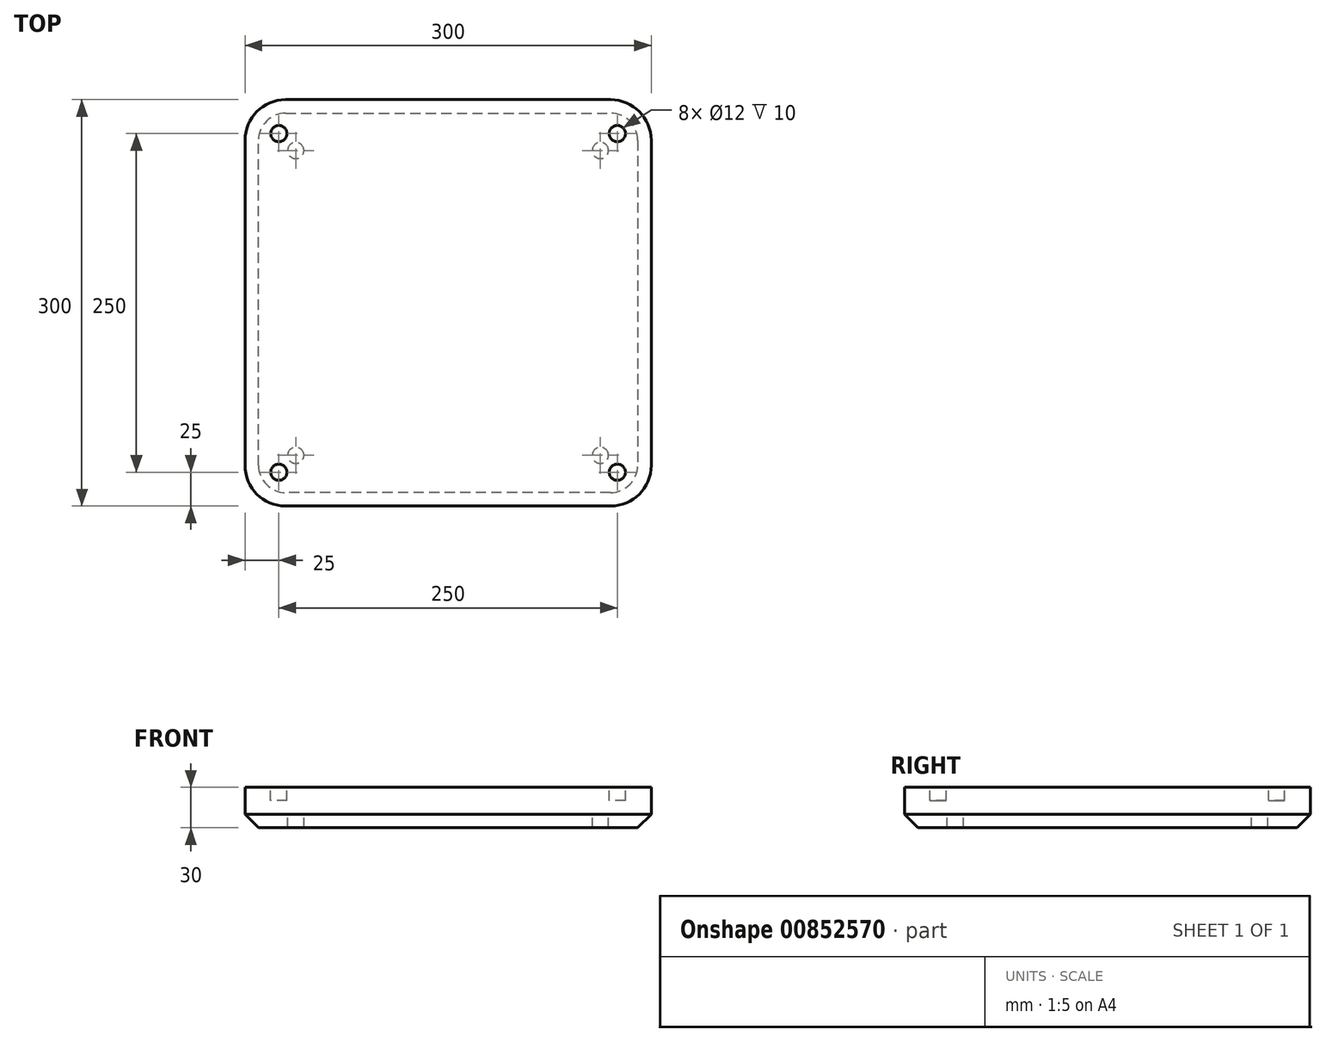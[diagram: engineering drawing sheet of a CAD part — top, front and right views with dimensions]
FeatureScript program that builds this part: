
annotation { "Feature Type Name" : "Feature", "Feature Type Description" : "" }
export const myFeature = defineFeature(function(context is Context, id is Id, definition is map)
    precondition{}
    {
        {
            var Q0;
            Q0=qCreatedBy(makeId("Top.planeOp"),FACE);
            var sketch = newSketch(context, id + "F0", { "sketchPlane" : qUnion([Q0])});
            skLineSegment(sketch, "E0.bottom", {"start": v(120, 150) * mm, "end": v(-120, 150) * mm});
            skLineSegment(sketch, "E0.top", {"start": v(120, -150) * mm, "end": v(-120, -150) * mm});
            skLineSegment(sketch, "E0.left", {"start": v(150, 120) * mm, "end": v(150, -120) * mm});
            skLineSegment(sketch, "E0.right", {"start": v(-150, 120) * mm, "end": v(-150, -120) * mm});
            skPoint(sketch, "E0.middle", {"position": v(0, 0) * mm});
            skPoint(sketch, "E1.visualSharp", {"position": v(-150, 150) * mm});
            skArc(sketch, "E1.filletArc", {"start": v(-120, 150) * mm, "mid": v(-141.21, 141.21) * mm, "end": v(-150, 120) * mm});
            skPoint(sketch, "E2.visualSharp", {"position": v(150, 150) * mm});
            skArc(sketch, "E2.filletArc", {"start": v(150, 120) * mm, "mid": v(141.21, 141.21) * mm, "end": v(120, 150) * mm});
            skPoint(sketch, "E3.visualSharp", {"position": v(150, -150) * mm});
            skArc(sketch, "E3.filletArc", {"start": v(120, -150) * mm, "mid": v(141.21, -141.21) * mm, "end": v(150, -120) * mm});
            skPoint(sketch, "E4.visualSharp", {"position": v(-150, -150) * mm});
            skArc(sketch, "E4.filletArc", {"start": v(-150, -120) * mm, "mid": v(-141.21, -141.21) * mm, "end": v(-120, -150) * mm});
            skCircle(sketch, "E5", {"center": v(-112.5, -112.5) * mm, "radius": 6 * mm});
            skCircle(sketch, "E6", {"center": v(-112.5, 112.5) * mm, "radius": 6 * mm});
            skCircle(sketch, "E7", {"center": v(112.5, 112.5) * mm, "radius": 6 * mm});
            skCircle(sketch, "E8", {"center": v(112.5, -112.5) * mm, "radius": 6 * mm});
            skCircle(sketch, "E9", {"center": v(125, 125) * mm, "radius": 6 * mm});
            skCircle(sketch, "E10", {"center": v(-125, 125) * mm, "radius": 6 * mm});
            skCircle(sketch, "E11", {"center": v(-125, -125) * mm, "radius": 6 * mm});
            skCircle(sketch, "E12", {"center": v(125, -125) * mm, "radius": 6 * mm});
            skSolve(sketch);
        }
        {
            var Q0;
            Q0=makeQuery(id+"F0.imprint","IMPRINT",FACE,{"disambiguationData":[TD([[makeQuery(id+"F0.imprint","IMPRINT",EDGE,{"derivedFrom":sQuery(id+"F0.wireOp",EDGE,"E0.bottom")}),1.0]])]});
            var Q1;
            Q1=makeQuery(id+"F0.imprint","IMPRINT",FACE,{"disambiguationData":[TD([[makeQuery(id+"F0.imprint","IMPRINT",EDGE,{"derivedFrom":sQuery(id+"F0.wireOp",EDGE,"E10")}),1.0]])]});
            var Q2;
            Q2=makeQuery(id+"F0.imprint","IMPRINT",FACE,{"disambiguationData":[TD([[makeQuery(id+"F0.imprint","IMPRINT",EDGE,{"derivedFrom":sQuery(id+"F0.wireOp",EDGE,"E9")}),1.0]])]});
            var Q3;
            Q3=makeQuery(id+"F0.imprint","IMPRINT",FACE,{"disambiguationData":[TD([[makeQuery(id+"F0.imprint","IMPRINT",EDGE,{"derivedFrom":sQuery(id+"F0.wireOp",EDGE,"E12")}),1.0]])]});
            var Q4;
            Q4=makeQuery(id+"F0.imprint","IMPRINT",FACE,{"disambiguationData":[TD([[makeQuery(id+"F0.imprint","IMPRINT",EDGE,{"derivedFrom":sQuery(id+"F0.wireOp",EDGE,"E11")}),1.0]])]});
            extrude(context, id + "F1", {"entities" : qUnion([Q0, Q1, Q2, Q3, Q4]), "oppositeDirection" : true, "depth" : 30 * mm, "offsetDistance" : 25 * mm});
        }
        {
            var Q0;
            Q0=makeQuery(id+"F1.opExtrude","CAP_EDGE",EDGE,{"disambiguationData":[OSD([sQuery(id+"F0.wireOp",EDGE,"E0.bottom")])],"isStart":false});
            chamfer(context, id + "F2", {"entities" : qUnion([Q0]), "chamferType" : ChamferType.OFFSET_ANGLE, "width" : 10 * mm, "oppositeDirection" : false, "angle" : 45 * degree, "tangentPropagation" : true});
        }
        {
            var Q0;
            Q0=makeQuery(id+"F0.imprint","IMPRINT",FACE,{"disambiguationData":[TD([[makeQuery(id+"F0.imprint","IMPRINT",EDGE,{"derivedFrom":sQuery(id+"F0.wireOp",EDGE,"E10")}),1.0]])]});
            var Q1;
            Q1=makeQuery(id+"F0.imprint","IMPRINT",FACE,{"disambiguationData":[TD([[makeQuery(id+"F0.imprint","IMPRINT",EDGE,{"derivedFrom":sQuery(id+"F0.wireOp",EDGE,"E9")}),1.0]])]});
            var Q2;
            Q2=makeQuery(id+"F0.imprint","IMPRINT",FACE,{"disambiguationData":[TD([[makeQuery(id+"F0.imprint","IMPRINT",EDGE,{"derivedFrom":sQuery(id+"F0.wireOp",EDGE,"E11")}),1.0]])]});
            var Q3;
            Q3=makeQuery(id+"F0.imprint","IMPRINT",FACE,{"disambiguationData":[TD([[makeQuery(id+"F0.imprint","IMPRINT",EDGE,{"derivedFrom":sQuery(id+"F0.wireOp",EDGE,"E12")}),1.0]])]});
            var Q4;
            Q4=sQuery(id+"F0.wireOp",EDGE,"E9");
            var Q5;
            Q5=sQuery(id+"F0.wireOp",EDGE,"E10");
            var Q6;
            Q6=sQuery(id+"F0.wireOp",EDGE,"E11");
            var Q7;
            Q7=sQuery(id+"F0.wireOp",EDGE,"E12");
            extrude(context, id + "F3", {"entities" : qUnion([Q0, Q1, Q2, Q3]), "operationType" : NewBodyOperationType.REMOVE, "surfaceEntities" : qUnion([Q4, Q5, Q6, Q7]), "oppositeDirection" : true, "depth" : 10 * mm, "offsetDistance" : 25 * mm});
        }
        {
            var Q0;
            Q0=makeQuery(id+"F0.imprint","IMPRINT",FACE,{"disambiguationData":[TD([[makeQuery(id+"F0.imprint","IMPRINT",EDGE,{"derivedFrom":sQuery(id+"F0.wireOp",EDGE,"E6")}),1.0]])]});
            var Q1;
            Q1=makeQuery(id+"F0.imprint","IMPRINT",FACE,{"disambiguationData":[TD([[makeQuery(id+"F0.imprint","IMPRINT",EDGE,{"derivedFrom":sQuery(id+"F0.wireOp",EDGE,"E7")}),1.0]])]});
            var Q2;
            Q2=makeQuery(id+"F0.imprint","IMPRINT",FACE,{"disambiguationData":[TD([[makeQuery(id+"F0.imprint","IMPRINT",EDGE,{"derivedFrom":sQuery(id+"F0.wireOp",EDGE,"E8")}),1.0]])]});
            var Q3;
            Q3=makeQuery(id+"F0.imprint","IMPRINT",FACE,{"disambiguationData":[TD([[makeQuery(id+"F0.imprint","IMPRINT",EDGE,{"derivedFrom":sQuery(id+"F0.wireOp",EDGE,"E5")}),1.0]])]});
            extrude(context, id + "F4", {"entities" : qUnion([Q0, Q1, Q2, Q3]), "operationType" : NewBodyOperationType.ADD, "oppositeDirection" : true, "depth" : 20 * mm, "offsetDistance" : 25 * mm});
        }
    });
